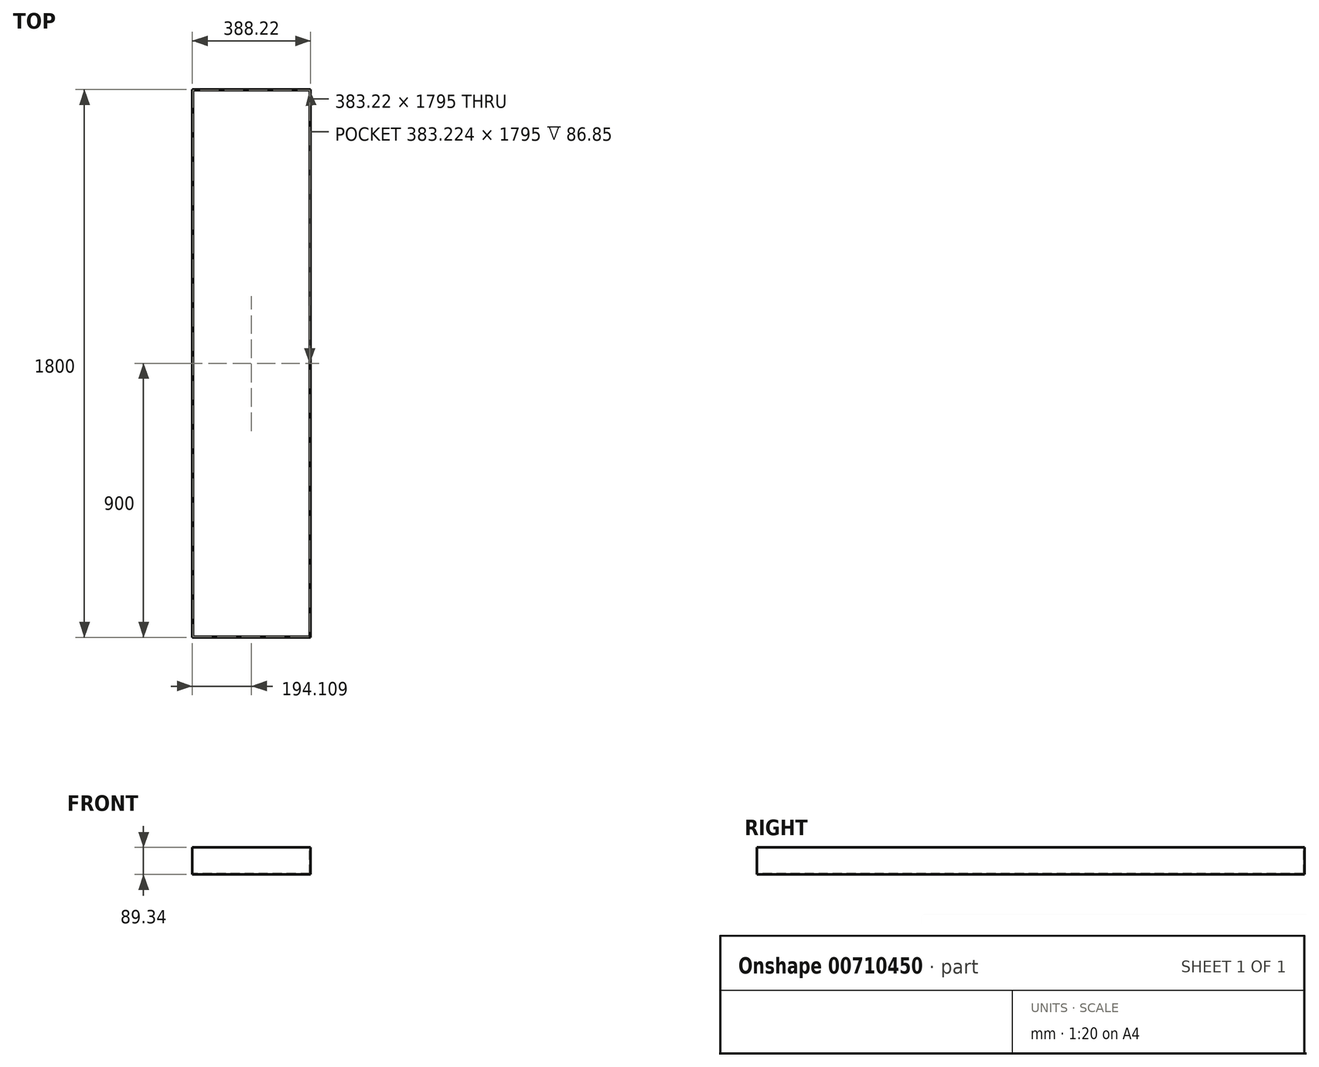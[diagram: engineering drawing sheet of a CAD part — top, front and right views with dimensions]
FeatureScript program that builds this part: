
annotation { "Feature Type Name" : "Feature", "Feature Type Description" : "" }
export const myFeature = defineFeature(function(context is Context, id is Id, definition is map)
    precondition{}
    {
        {
            var Q0;
            Q0=qCreatedBy(makeId("Front.planeOp"),FACE);
            var sketch = newSketch(context, id + "F0", { "sketchPlane" : qUnion([Q0])});
            skLineSegment(sketch, "E0.bottom", {"start": v(174.21, -44.67) * mm, "end": v(-214.01, -44.67) * mm});
            skLineSegment(sketch, "E0.top", {"start": v(174.21, 44.67) * mm, "end": v(-214.01, 44.67) * mm});
            skLineSegment(sketch, "E0.left", {"start": v(174.21, -44.67) * mm, "end": v(174.21, 44.67) * mm});
            skLineSegment(sketch, "E0.right", {"start": v(-214.01, -44.67) * mm, "end": v(-214.01, 44.67) * mm});
            skPoint(sketch, "E0.middle", {"position": v(-19.9, 0) * mm});
            skSolve(sketch);
        }
        {
            var Q0;
            Q0=makeQuery(id+"F0.imprint","IMPRINT",FACE,{"disambiguationData":[TD([[makeQuery(id+"F0.imprint","IMPRINT",EDGE,{"derivedFrom":sQuery(id+"F0.wireOp",EDGE,"E0.bottom")}),-1.0]])]});
            extrude(context, id + "F1", {"entities" : qUnion([Q0]), "endBound" : BoundingType.SYMMETRIC, "oppositeDirection" : true, "depth" : 1800 * mm, "offsetDistance" : 25 * mm});
        }
        {
            var Q0;
            Q0=makeQuery(id+"F1.opExtrude","SWEPT_FACE",FACE,{"disambiguationData":[OSD([sQuery(id+"F0.wireOp",EDGE,"E0.top")])]});
            shell(context, id + "F2", {"entities" : qUnion([Q0]), "thickness" : 2.5 * mm});
        }
    });
